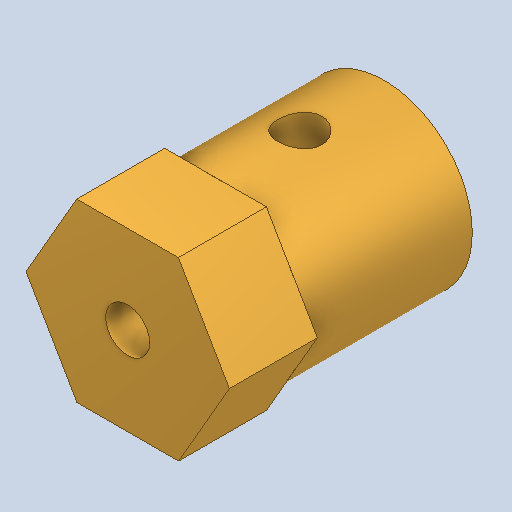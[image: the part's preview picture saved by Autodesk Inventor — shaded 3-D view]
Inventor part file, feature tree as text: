
AUTODESK INVENTOR PART (.ipt)
format: ipt  version: 2025.2 (Build 292293000, 293)  size: 281,600 bytes
history: native  units: mm
features: extrude x5, sketch x5
ambient origin geometry x8: Origin, YZ Plane, XZ Plane, XY Plane, X Axis, Y Axis, Z Axis, Center Point
bodies: Body1 (feature_tree)
feature tree (10):
  extrude  "Extrusion2"  Depth=11.5mm TaperAngle=0.0deg
  sketch  "Sketch3"  dims[d6=6.0mm d7=6.0mm d8=0.0mm]
  sketch  "Sketch4"  dims[d9=6.0mm d10=0.0mm d11=3.0mm]
  extrude  "Extrusion3"  Depth=6.0mm TaperAngle=0.0deg
  extrude  "Extrusion4"  Depth=3.0mm
  extrude  "Extrusion5"  Depth=3.0mm
  extrude  "Extrusion6"  Depth=10.0mm
  sketch  "Sketch2"  dims[d3=12.0mm d4=11.5mm d5=0.0mm]
  sketch  "Sketch5"  dims[d12=0.0mm d13=0.0mm d14=3.0mm]
  sketch  "Sketch6"  dims[d15=10.0mm d16=0.0mm d19=0.5mm d20=0.872665mm d21=0.5mm d22=0.872665mm]
